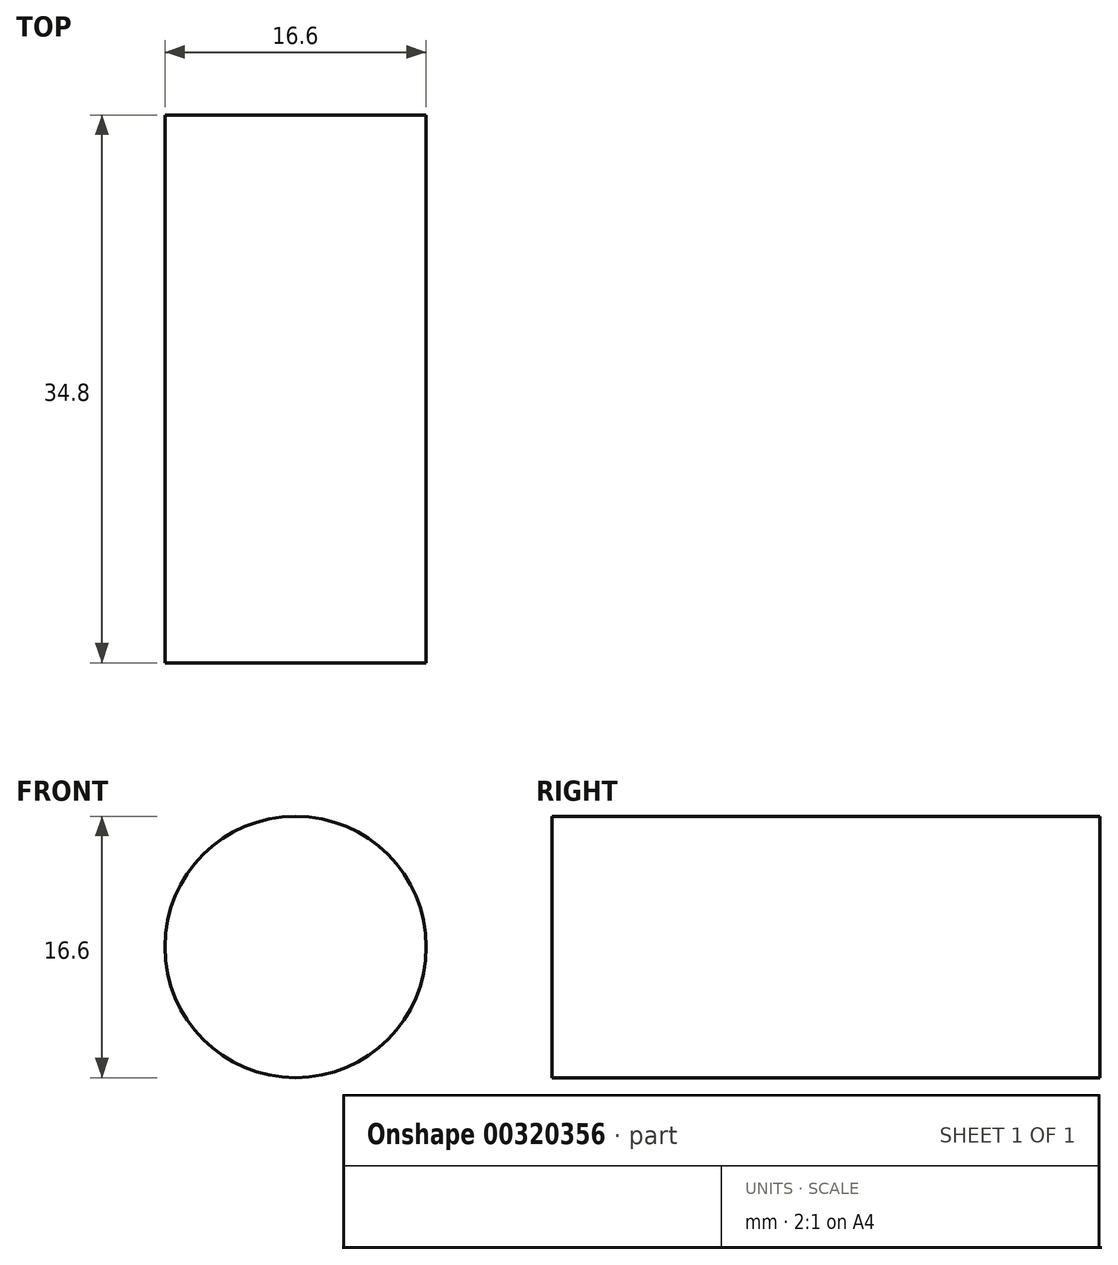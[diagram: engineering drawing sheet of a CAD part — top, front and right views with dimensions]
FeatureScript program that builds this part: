
annotation { "Feature Type Name" : "Feature", "Feature Type Description" : "" }
export const myFeature = defineFeature(function(context is Context, id is Id, definition is map)
    precondition{}
    {
        {
            var Q0;
            Q0=qCreatedBy(makeId("Front.planeOp"),FACE);
            var sketch = newSketch(context, id + "F0", { "sketchPlane" : qUnion([Q0])});
            skCircle(sketch, "E0", {"center": v(0, 0) * mm, "radius": 8.3 * mm});
            skSolve(sketch);
        }
        {
            var Q0;
            Q0 = qSketchRegion(id + "F0", true);
            extrude(context, id + "F1", {"entities" : qUnion([Q0]), "depth" : 17.4 * mm, "hasSecondDirection" : true, "secondDirectionOppositeDirection" : true, "secondDirectionDepth" : 17.4 * mm});
        }
    });
